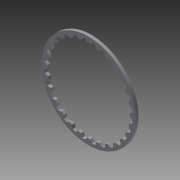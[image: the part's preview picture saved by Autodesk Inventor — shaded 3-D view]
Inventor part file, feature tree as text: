
AUTODESK INVENTOR PART (.ipt)
format: ipt  version: 2013 (Build 170138000, 138)  size: 224,768 bytes
history: native  units: in
note: dims shown in document units (in); Inventor stores cm internally (conversion verified against a paired STEP export)
features: extrude x1, sketch x1
ambient origin geometry x8: Origin, YZ Plane, XZ Plane, XY Plane, X Axis, Y Axis, Z Axis, Center Point
bodies: Solid1 (feature_tree)
feature tree (2):
  extrude  "Extrusion1"  Depth=0.071in
  sketch  "Sketch1"  dims[d0=0.0625in d2=0.071in d3=11.0236in d5=360.0deg d7=120.0deg d8=0.0625in d9=0.0625in d10=0.0625in d11=0.0in]
